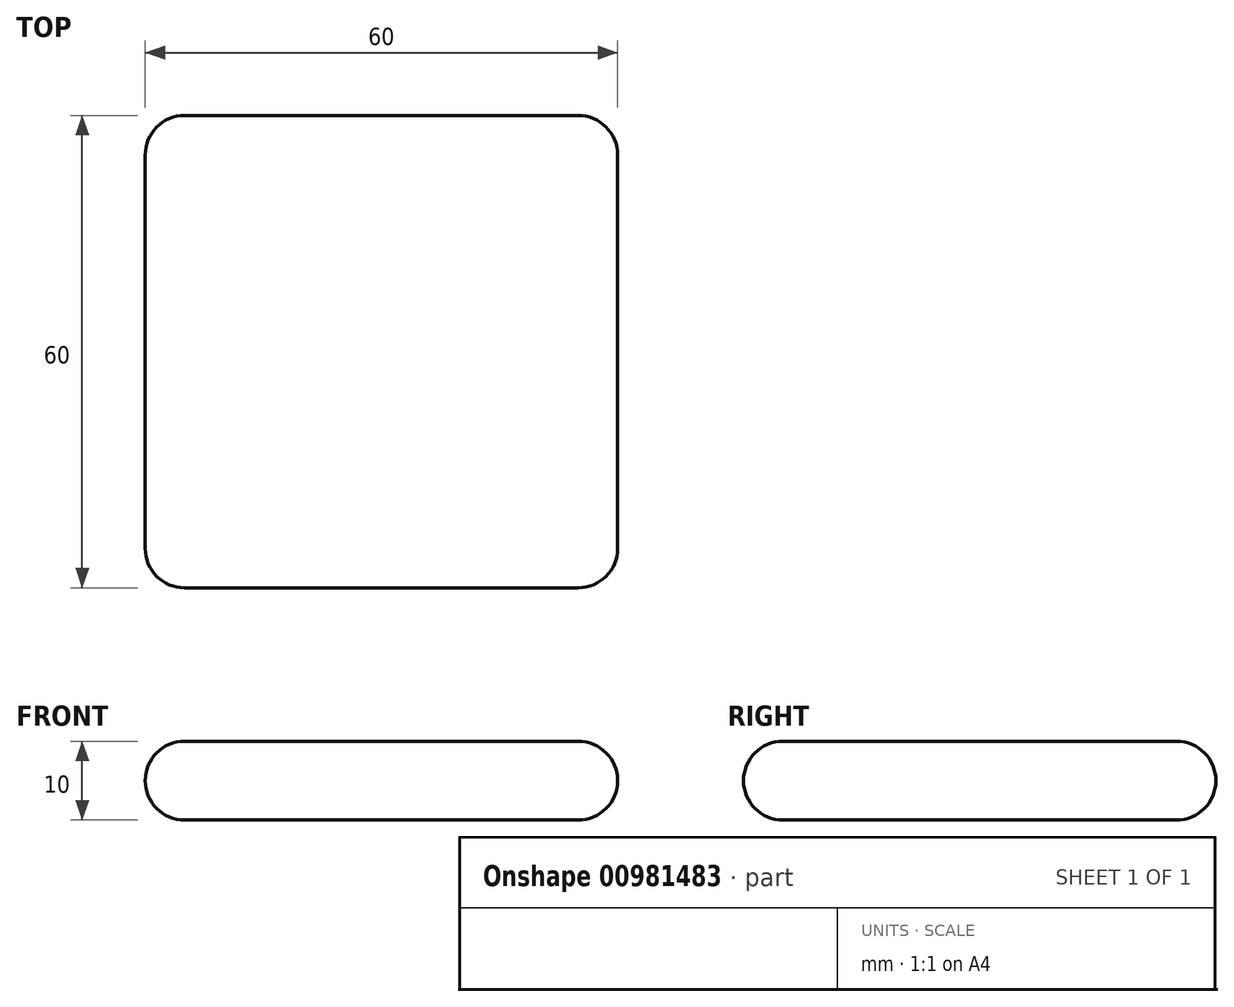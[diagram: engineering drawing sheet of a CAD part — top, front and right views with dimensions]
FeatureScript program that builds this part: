
annotation { "Feature Type Name" : "Feature", "Feature Type Description" : "" }
export const myFeature = defineFeature(function(context is Context, id is Id, definition is map)
    precondition{}
    {
        {
            var Q0;
            Q0=qCreatedBy(makeId("Top.planeOp"),FACE);
            var sketch = newSketch(context, id + "F0", { "sketchPlane" : qUnion([Q0])});
            skLineSegment(sketch, "E0.bottom", {"start": v(-28.61, 41.27) * mm, "end": v(31.39, 41.27) * mm});
            skLineSegment(sketch, "E0.top", {"start": v(-28.61, -18.73) * mm, "end": v(31.39, -18.73) * mm});
            skLineSegment(sketch, "E0.left", {"start": v(-28.61, 41.27) * mm, "end": v(-28.61, -18.73) * mm});
            skLineSegment(sketch, "E0.right", {"start": v(31.39, 41.27) * mm, "end": v(31.39, -18.73) * mm});
            skSolve(sketch);
        }
        {
            var Q0;
            Q0=makeQuery(id+"F0.imprint","IMPRINT",FACE,{"disambiguationData":[TD([[makeQuery(id+"F0.imprint","IMPRINT",EDGE,{"derivedFrom":sQuery(id+"F0.wireOp",EDGE,"E0.bottom")}),-1.0]])]});
            extrude(context, id + "F1", {"entities" : qUnion([Q0]), "depth" : 10 * mm, "offsetDistance" : 25 * mm});
        }
        {
            var Q0;
            Q0=makeQuery(id+"F1.opExtrude","SWEPT_FACE",FACE,{"disambiguationData":[OSD([sQuery(id+"F0.wireOp",EDGE,"E0.left")])]});
            var Q1;
            Q1=makeQuery(id+"F1.opExtrude","SWEPT_FACE",FACE,{"disambiguationData":[OSD([sQuery(id+"F0.wireOp",EDGE,"E0.bottom")])]});
            var Q2;
            Q2=makeQuery(id+"F1.opExtrude","SWEPT_FACE",FACE,{"disambiguationData":[OSD([sQuery(id+"F0.wireOp",EDGE,"E0.top")])]});
            var Q3;
            Q3=makeQuery(id+"F1.opExtrude","SWEPT_FACE",FACE,{"disambiguationData":[OSD([sQuery(id+"F0.wireOp",EDGE,"E0.right")])]});
            fillet(context, id + "F2", {"entities" : qUnion([Q0, Q1, Q2, Q3]), "radius" : 5 * mm, "tangentPropagation" : true, "allowEdgeOverflow" : false});
        }
    });
